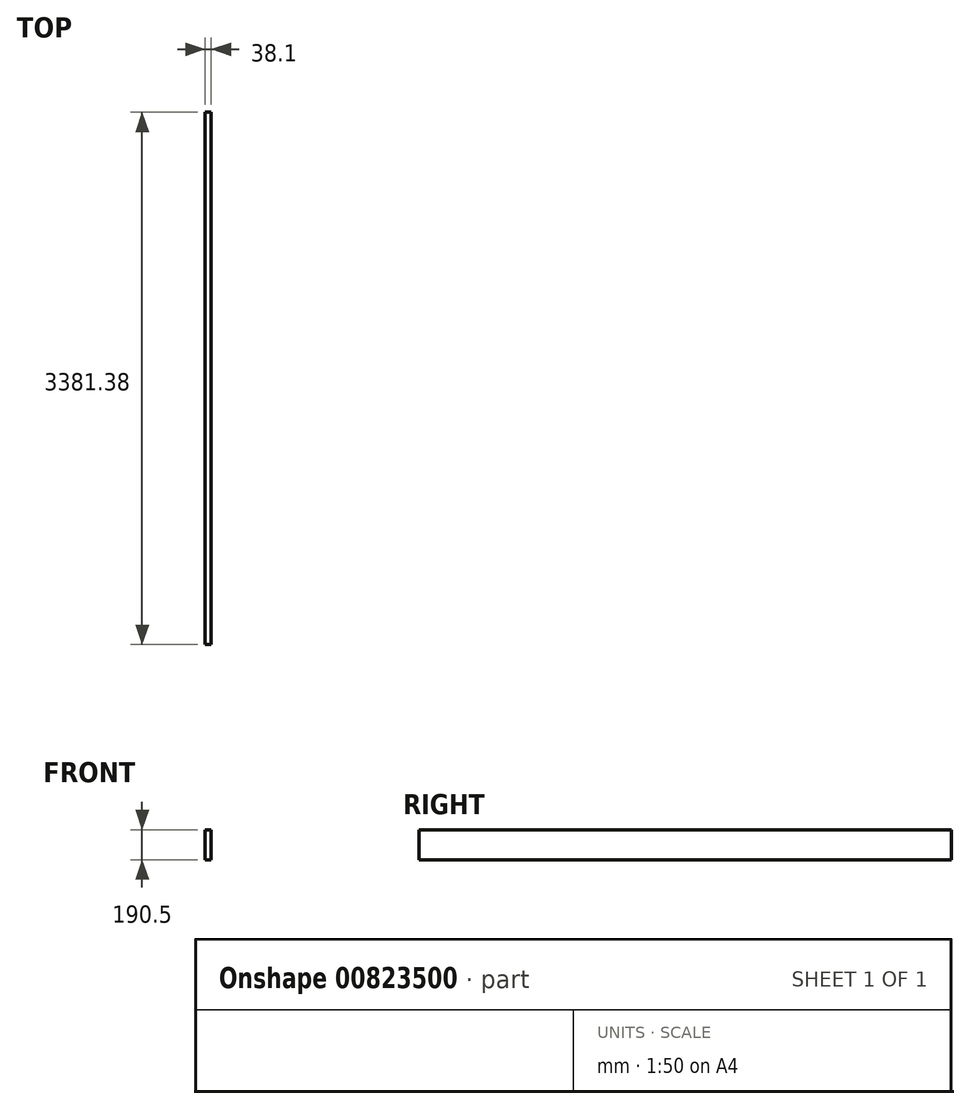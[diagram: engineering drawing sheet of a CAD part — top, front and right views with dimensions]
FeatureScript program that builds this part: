
annotation { "Feature Type Name" : "Feature", "Feature Type Description" : "" }
export const myFeature = defineFeature(function(context is Context, id is Id, definition is map)
    precondition{}
    {
        {
            var Q0;
            Q0=qCreatedBy(makeId("Front.planeOp"),FACE);
            var sketch = newSketch(context, id + "F0", { "sketchPlane" : qUnion([Q0])});
            skLineSegment(sketch, "E0.bottom", {"start": v(0, 0) * mm, "end": v(38.1, 0) * mm});
            skLineSegment(sketch, "E0.top", {"start": v(0, 190.5) * mm, "end": v(38.1, 190.5) * mm});
            skLineSegment(sketch, "E0.left", {"start": v(0, 0) * mm, "end": v(0, 190.5) * mm});
            skLineSegment(sketch, "E0.right", {"start": v(38.1, 0) * mm, "end": v(38.1, 190.5) * mm});
            skSolve(sketch);
        }
        {
            var Q0;
            Q0=qSketchRegion(id+"F0",true);
            extrude(context, id + "F1", {"entities" : qUnion([Q0]), "depth" : 3381.38 * mm, "offsetDistance" : 25.4 * mm});
        }
    });
